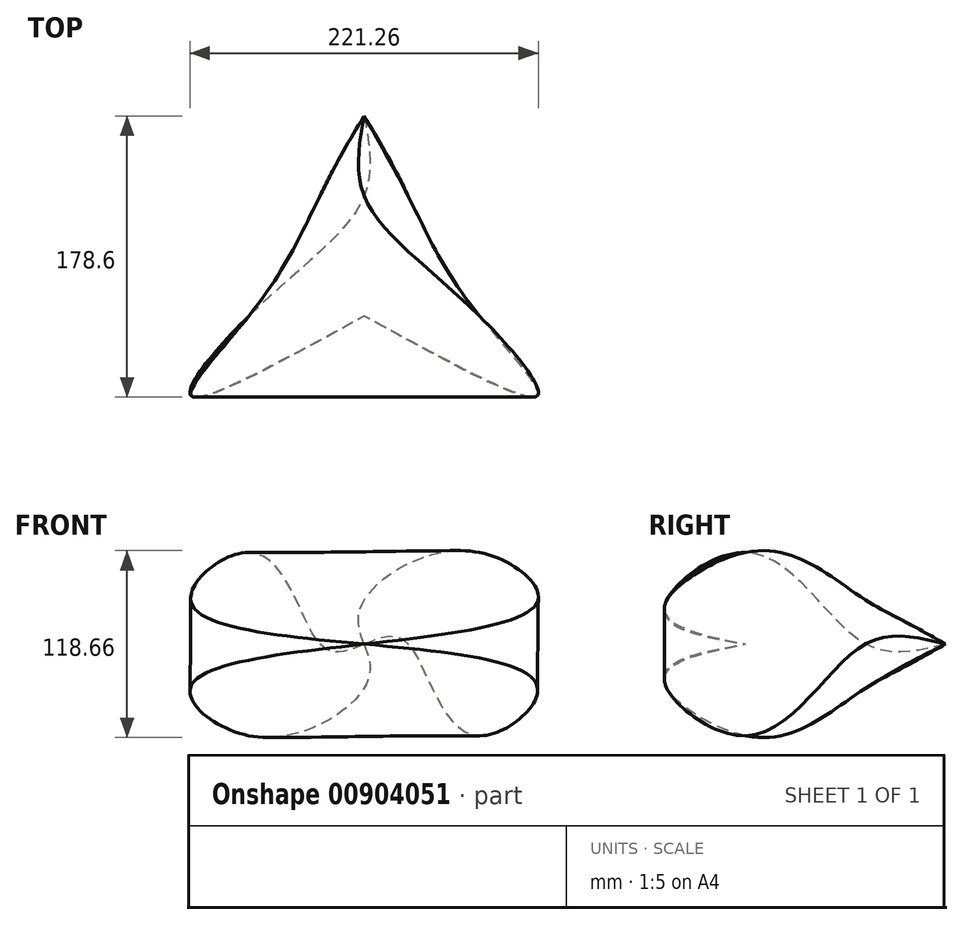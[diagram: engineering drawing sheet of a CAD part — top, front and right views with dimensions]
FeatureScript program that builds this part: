
annotation { "Feature Type Name" : "Feature", "Feature Type Description" : "" }
export const myFeature = defineFeature(function(context is Context, id is Id, definition is map)
    precondition{}
    {
        {
            var Q0;
            Q0=qCreatedBy(makeId("Front.planeOp"),FACE);
            cPlane(context, id + "F0", {"entities" : qUnion([Q0]), "cplaneType" : CPlaneType.OFFSET, "offset" : 50.8 * mm, "width" : 152.4 * mm, "height" : 152.4 * mm});
        }
        {
            var Q0;
            Q0=qCreatedBy(id+"F0.planeOp",FACE);
            cPlane(context, id + "F1", {"entities" : qUnion([Q0]), "cplaneType" : CPlaneType.OFFSET, "offset" : 76.2 * mm, "width" : 152.4 * mm, "height" : 152.4 * mm});
        }
        {
            var Q0;
            Q0=qCreatedBy(id+"F1.planeOp",FACE);
            cPlane(context, id + "F2", {"entities" : qUnion([Q0]), "cplaneType" : CPlaneType.OFFSET, "offset" : 50.8 * mm, "width" : 152.4 * mm, "height" : 152.4 * mm});
        }
        {
            var Q0;
            Q0=qCreatedBy(makeId("Front.planeOp"),FACE);
            var sketch = newSketch(context, id + "F3", { "sketchPlane" : qUnion([Q0])});
            skPoint(sketch, "E0", {"position": v(0, 0) * mm});
            skSolve(sketch);
        }
        {
            var Q0;
            Q0=qCreatedBy(id+"F0.planeOp",FACE);
            var sketch = newSketch(context, id + "F4", { "sketchPlane" : qUnion([Q0])});
            skCircle(sketch, "E1", {"center": v(0, 0) * mm, "radius": 28 * mm});
            skSolve(sketch);
        }
        {
            var Q0;
            Q0=qCreatedBy(id+"F1.planeOp",FACE);
            var sketch = newSketch(context, id + "F5", { "sketchPlane" : qUnion([Q0])});
            skLineSegment(sketch, "E2.bottom", {"start": v(73.18, -58.19) * mm, "end": v(-73.18, -58.19) * mm});
            skLineSegment(sketch, "E2.top", {"start": v(73.18, 58.19) * mm, "end": v(-73.18, 58.19) * mm});
            skLineSegment(sketch, "E2.left", {"start": v(73.18, -58.19) * mm, "end": v(73.18, 58.19) * mm});
            skLineSegment(sketch, "E2.right", {"start": v(-73.18, -58.19) * mm, "end": v(-73.18, 58.19) * mm});
            skPoint(sketch, "E2.middle", {"position": v(0, 0) * mm});
            skSolve(sketch);
        }
        {
            var Q0;
            Q0=qCreatedBy(id+"F2.planeOp",FACE);
            var sketch = newSketch(context, id + "F6", { "sketchPlane" : qUnion([Q0])});
            skLineSegment(sketch, "E3.bottom", {"start": v(109.7, -26.13) * mm, "end": v(-109.7, -26.13) * mm});
            skLineSegment(sketch, "E3.top", {"start": v(109.7, 26.13) * mm, "end": v(-109.7, 26.13) * mm});
            skLineSegment(sketch, "E3.left", {"start": v(109.7, -26.13) * mm, "end": v(109.7, 26.13) * mm});
            skLineSegment(sketch, "E3.right", {"start": v(-109.7, -26.13) * mm, "end": v(-109.7, 26.13) * mm});
            skPoint(sketch, "E3.middle", {"position": v(0, 0) * mm});
            skSolve(sketch);
        }
        {
            var Q0;
            Q0=sQuery(id+"F3.wireOp",VERTEX,"E0");
            var Q1;
            Q1=makeQuery(id+"F4.imprint","IMPRINT",FACE,{"disambiguationData":[TD([[makeQuery(id+"F4.imprint","IMPRINT",EDGE,{"derivedFrom":sQuery(id+"F4.wireOp",EDGE,"E1")}),1.0]])]});
            var Q2;
            Q2=makeQuery(id+"F5.imprint","IMPRINT",FACE,{"disambiguationData":[TD([[makeQuery(id+"F5.imprint","IMPRINT",EDGE,{"derivedFrom":sQuery(id+"F5.wireOp",EDGE,"E2.bottom")}),-1.0]])]});
            var Q3;
            Q3=makeQuery(id+"F6.imprint","IMPRINT",FACE,{"disambiguationData":[TD([[makeQuery(id+"F6.imprint","IMPRINT",EDGE,{"derivedFrom":sQuery(id+"F6.wireOp",EDGE,"E3.bottom")}),-1.0]])]});
            var Q4;
            Q4=sQuery(id+"F5.wireOp",VERTEX,"E2.middle");
            loft(context, id + "F7", {"sheetProfilesArray" : [{ "sheetProfileEntities" : qUnion([Q0]) }, { "sheetProfileEntities" : qUnion([Q1]) }, { "sheetProfileEntities" : qUnion([Q2]) }, { "sheetProfileEntities" : qUnion([Q3]) }, { "sheetProfileEntities" : qUnion([Q4]) }]});
        }
    });
